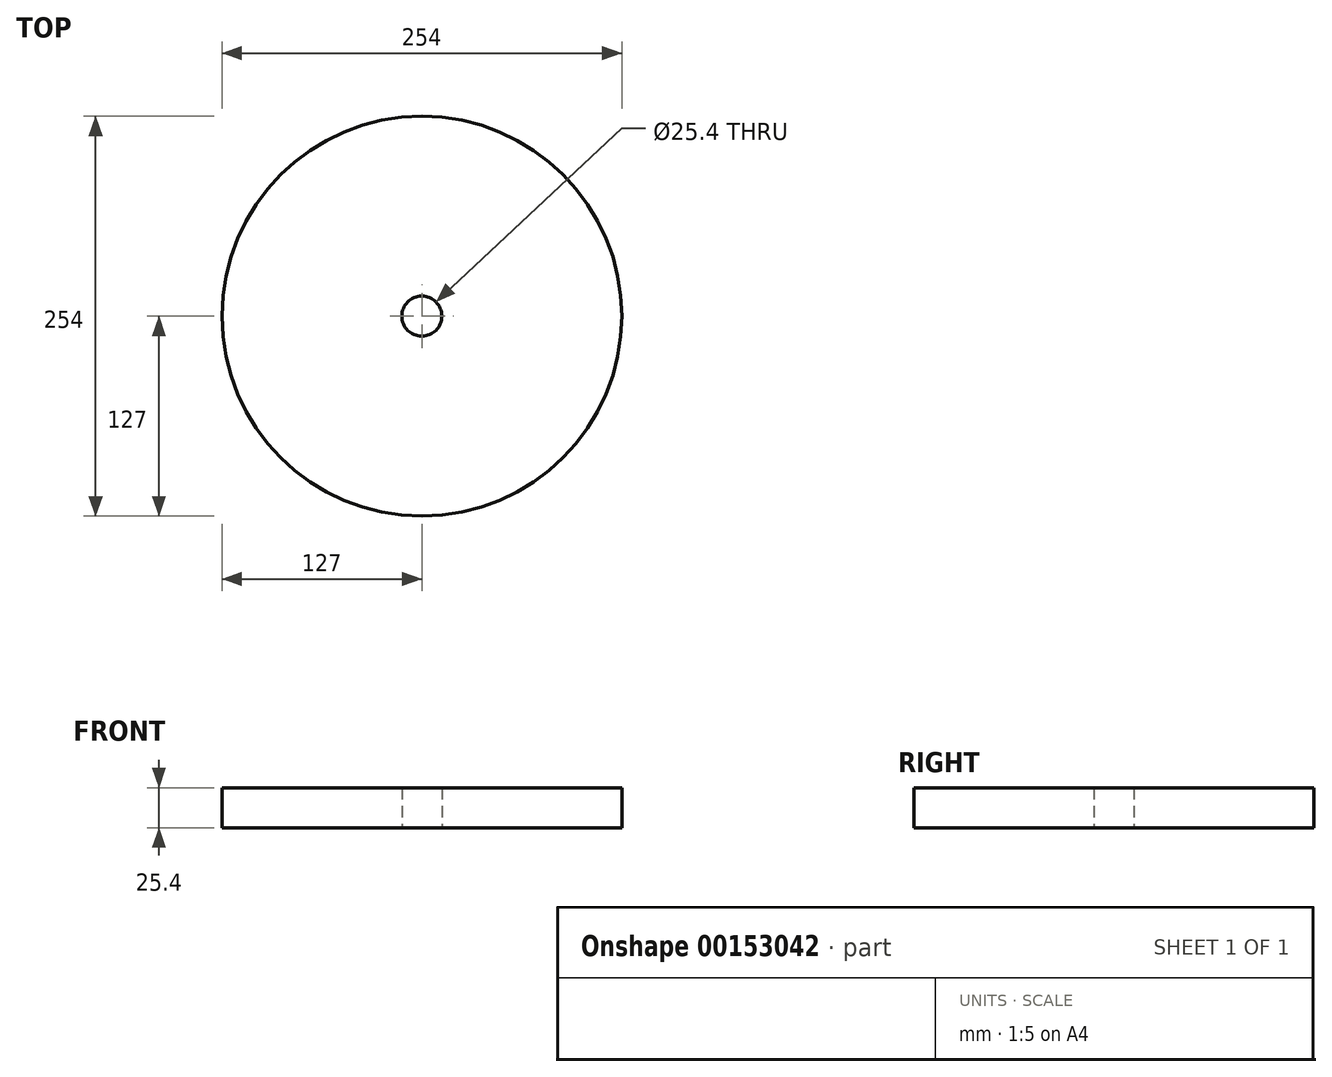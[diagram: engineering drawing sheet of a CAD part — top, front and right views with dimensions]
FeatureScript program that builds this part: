
annotation { "Feature Type Name" : "Feature", "Feature Type Description" : "" }
export const myFeature = defineFeature(function(context is Context, id is Id, definition is map)
    precondition{}
    {
        {
            var Q0;
            Q0=qCreatedBy(makeId("Top.planeOp"),FACE);
            var sketch = newSketch(context, id + "F0", { "sketchPlane" : qUnion([Q0])});
            skCircle(sketch, "E0", {"center": v(0, 0) * mm, "radius": 127 * mm});
            skCircle(sketch, "E1", {"center": v(0, 0) * mm, "radius": 12.7 * mm});
            skSolve(sketch);
        }
        {
            var Q0;
            Q0=makeQuery(id+"F0.imprint","IMPRINT",FACE,{"disambiguationData":[TD([[makeQuery(id+"F0.imprint","IMPRINT",EDGE,{"derivedFrom":sQuery(id+"F0.wireOp",EDGE,"E0")}),1.0]])]});
            extrude(context, id + "F1", {"entities" : qUnion([Q0]), "depth" : 25.4 * mm});
        }
    });
